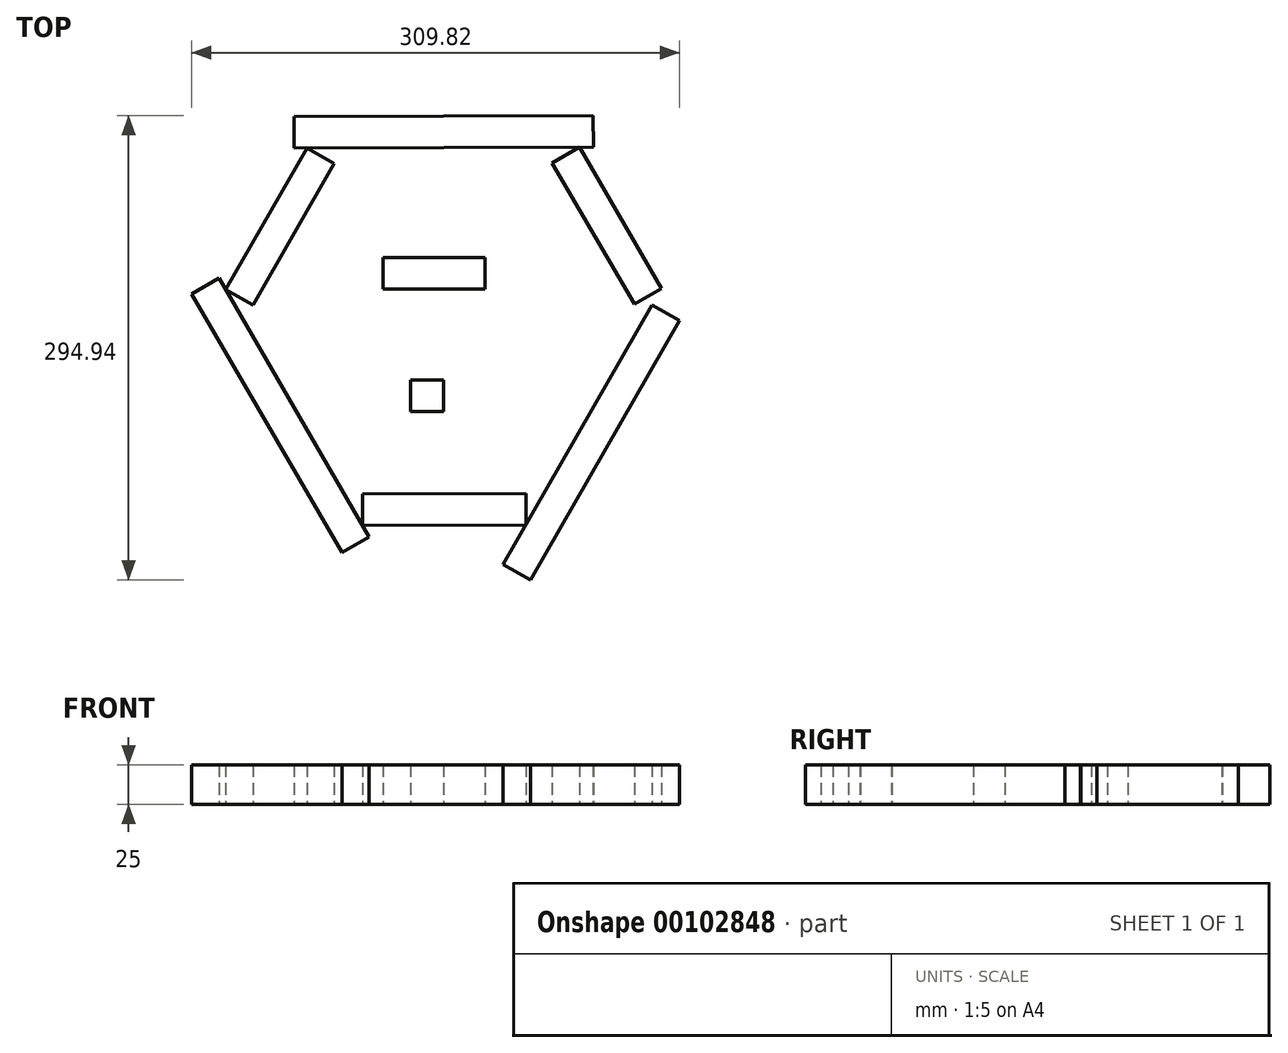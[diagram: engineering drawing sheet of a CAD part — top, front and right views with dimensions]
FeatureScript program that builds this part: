
annotation { "Feature Type Name" : "Feature", "Feature Type Description" : "" }
export const myFeature = defineFeature(function(context is Context, id is Id, definition is map)
    precondition{}
    {
        {
            var Q0;
            Q0=qCreatedBy(makeId("Top.planeOp"),FACE);
            var sketch = newSketch(context, id + "F0", { "sketchPlane" : qUnion([Q0])});
            skLineSegment(sketch, "E0", {"start": v(0, 129.9) * mm, "end": v(-95, 129.66) * mm});
            skLineSegment(sketch, "E1", {"start": v(-95, 129.66) * mm, "end": v(-94.95, 109.66) * mm});
            skLineSegment(sketch, "E2", {"start": v(-94.95, 109.66) * mm, "end": v(95.05, 110.15) * mm});
            skLineSegment(sketch, "E3", {"start": v(95.05, 110.15) * mm, "end": v(95, 130.15) * mm});
            skLineSegment(sketch, "E4", {"start": v(95, 130.15) * mm, "end": v(0, 129.9) * mm});
            skLineSegment(sketch, "E5", {"start": v(37.86, -154.83) * mm, "end": v(55.2, -164.79) * mm});
            skLineSegment(sketch, "E6", {"start": v(55.2, -164.79) * mm, "end": v(102.5, -82.4) * mm});
            skLineSegment(sketch, "E7", {"start": v(138.4, 20.36) * mm, "end": v(86.26, 110.13) * mm});
            skLineSegment(sketch, "E8", {"start": v(86.26, 110.13) * mm, "end": v(68.97, 100.08) * mm});
            skLineSegment(sketch, "E9", {"start": v(138.4, 20.36) * mm, "end": v(121.1, 10.31) * mm});
            skLineSegment(sketch, "E10", {"start": v(121.1, 10.31) * mm, "end": v(68.97, 100.08) * mm});
            skLineSegment(sketch, "E11.0", {"start": v(-63.77, 109.74) * mm, "end": v(63.15, 110.1) * mm});
            skLineSegment(sketch, "E12", {"start": v(-112.33, -65.24) * mm, "end": v(-160.04, 16.9) * mm});
            skLineSegment(sketch, "E13", {"start": v(-160.04, 16.9) * mm, "end": v(-142.75, 26.95) * mm});
            skLineSegment(sketch, "E14", {"start": v(-112.33, -65.24) * mm, "end": v(-64.62, -147.4) * mm});
            skLineSegment(sketch, "E15", {"start": v(-64.62, -147.4) * mm, "end": v(-47.33, -137.35) * mm});
            skLineSegment(sketch, "E16", {"start": v(-47.33, -137.35) * mm, "end": v(-142.75, 26.95) * mm});
            skLineSegment(sketch, "E17", {"start": v(-51.57, -130.04) * mm, "end": v(52.24, -129.77) * mm});
            skLineSegment(sketch, "E18", {"start": v(52.24, -129.77) * mm, "end": v(52.2, -109.77) * mm});
            skLineSegment(sketch, "E19", {"start": v(-51.57, -130.04) * mm, "end": v(-51.62, -110.04) * mm});
            skLineSegment(sketch, "E20", {"start": v(-51.62, -110.04) * mm, "end": v(52.2, -109.77) * mm});
            skLineSegment(sketch, "E21", {"start": v(-86.83, 109.68) * mm, "end": v(-138.5, 19.64) * mm});
            skLineSegment(sketch, "E22", {"start": v(-138.5, 19.64) * mm, "end": v(-121.16, 9.69) * mm});
            skLineSegment(sketch, "E23", {"start": v(-86.83, 109.68) * mm, "end": v(-69.48, 99.73) * mm});
            skLineSegment(sketch, "E24", {"start": v(-69.48, 99.73) * mm, "end": v(-121.16, 9.69) * mm});
            skLineSegment(sketch, "E25", {"start": v(55.2, -164.79) * mm, "end": v(149.78, 0) * mm});
            skLineSegment(sketch, "E26", {"start": v(149.78, 0) * mm, "end": v(132.43, 9.96) * mm});
            skLineSegment(sketch, "E27", {"start": v(132.43, 9.96) * mm, "end": v(37.86, -154.83) * mm});
            skLineSegment(sketch, "E28", {"start": v(52.24, -129.77) * mm, "end": v(150.18, 40.88) * mm, "construction": true});
            skLineSegment(sketch, "E29.bottom", {"start": v(-38.6, 40) * mm, "end": v(26.4, 40) * mm});
            skLineSegment(sketch, "E29.top", {"start": v(-38.6, 20) * mm, "end": v(26.4, 20) * mm});
            skLineSegment(sketch, "E29.left", {"start": v(-38.6, 40) * mm, "end": v(-38.6, 20) * mm});
            skLineSegment(sketch, "E29.right", {"start": v(26.4, 40) * mm, "end": v(26.4, 20) * mm});
            skLineSegment(sketch, "E30.bottom", {"start": v(-21, -37.95) * mm, "end": v(0, -37.95) * mm});
            skLineSegment(sketch, "E30.top", {"start": v(-21, -57.95) * mm, "end": v(0, -57.95) * mm});
            skLineSegment(sketch, "E30.left", {"start": v(-21, -37.95) * mm, "end": v(-21, -57.95) * mm});
            skLineSegment(sketch, "E30.right", {"start": v(0, -37.95) * mm, "end": v(0, -57.95) * mm});
            skSolve(sketch);
        }
        {
            var Q0;
            Q0=makeQuery(id+"F0.imprint","IMPRINT",FACE,{"disambiguationData":[TD([[makeQuery(id+"F0.imprint","IMPRINT",EDGE,{"derivedFrom":sQuery(id+"F0.wireOp",EDGE,"E21")}),1.0]])]});
            var Q1;
            Q1=makeQuery(id+"F0.imprint","IMPRINT",FACE,{"disambiguationData":[TD([[makeQuery(id+"F0.imprint","IMPRINT",EDGE,{"derivedFrom":sQuery(id+"F0.wireOp",EDGE,"E0")}),1.0]])]});
            var Q2;
            Q2=makeQuery(id+"F0.imprint","IMPRINT",FACE,{"disambiguationData":[TD([[makeQuery(id+"F0.imprint","IMPRINT",EDGE,{"derivedFrom":sQuery(id+"F0.wireOp",EDGE,"E7")}),1.0]])]});
            var Q3;
            Q3=makeQuery(id+"F0.imprint","IMPRINT",FACE,{"disambiguationData":[TD([[makeQuery(id+"F0.imprint","IMPRINT",EDGE,{"derivedFrom":sQuery(id+"F0.wireOp",EDGE,"YU4wnqPE-PLdM-E96o-vomo-rtOJtL2YFN7a")}),1.0]])]});
            var Q4;
            Q4=makeQuery(id+"F0.imprint","IMPRINT",FACE,{"disambiguationData":[TD([[makeQuery(id+"F0.imprint","IMPRINT",EDGE,{"derivedFrom":sQuery(id+"F0.wireOp",EDGE,"E17")}),1.0]])]});
            var Q5;
            Q5=makeQuery(id+"F0.imprint","IMPRINT",FACE,{"disambiguationData":[TD([[makeQuery(id+"F0.imprint","IMPRINT",EDGE,{"derivedFrom":sQuery(id+"F0.wireOp",EDGE,"E12")}),-1.0]])]});
            extrude(context, id + "F1", {"entities" : qUnion([Q0, Q1, Q2, Q3, Q4, Q5]), "depth" : 25 * mm});
        }
        {
            var Q0;
            {var subQ4=sQuery(id+"F0.wireOp",EDGE,"E5");Q0=makeQuery(id+"F0.imprint","IMPRINT",FACE,{"disambiguationData":[TD([[makeQuery(id+"F0.imprint","IMPRINT",EDGE,{"derivedFrom":subQ4}),1.0]])]});}
            extrude(context, id + "F2", {"entities" : qUnion([Q0]), "depth" : 25 * mm});
        }
        {
            var Q0;
            Q0=makeQuery(id+"F0.imprint","IMPRINT",FACE,{"disambiguationData":[TD([[makeQuery(id+"F0.imprint","IMPRINT",EDGE,{"derivedFrom":sQuery(id+"F0.wireOp",EDGE,"E29.bottom")}),-1.0]])]});
            var Q1;
            Q1=makeQuery(id+"F0.imprint","IMPRINT",FACE,{"disambiguationData":[TD([[makeQuery(id+"F0.imprint","IMPRINT",EDGE,{"derivedFrom":sQuery(id+"F0.wireOp",EDGE,"E30.bottom")}),-1.0]])]});
            extrude(context, id + "F3", {"entities" : qUnion([Q0, Q1]), "depth" : 25 * mm});
        }
    });
